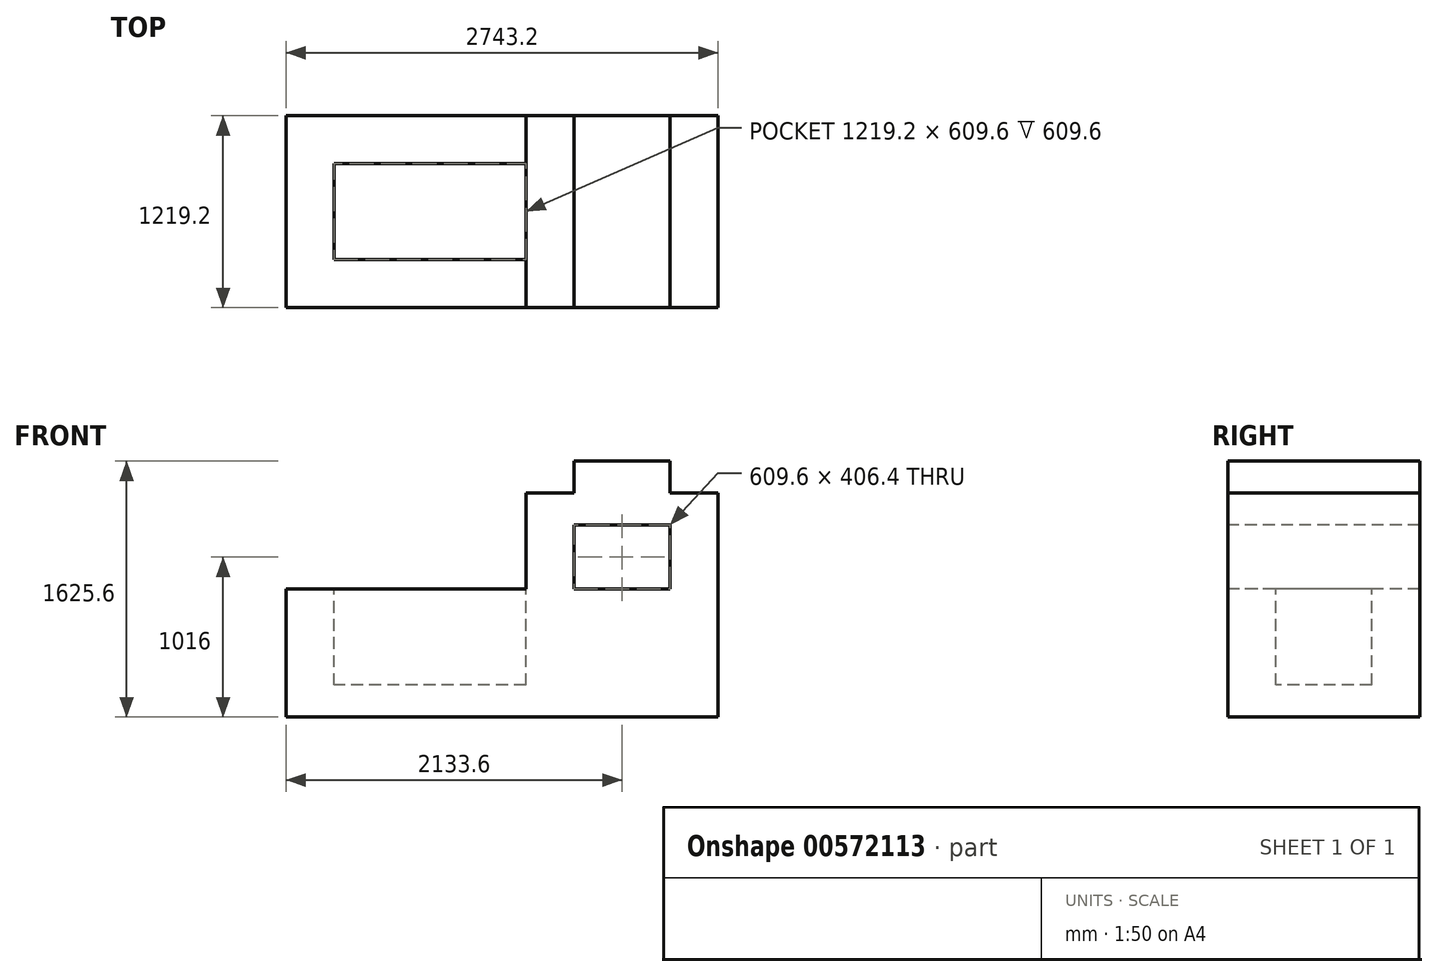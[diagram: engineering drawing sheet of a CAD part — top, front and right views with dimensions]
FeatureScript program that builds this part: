
annotation { "Feature Type Name" : "Feature", "Feature Type Description" : "" }
export const myFeature = defineFeature(function(context is Context, id is Id, definition is map)
    precondition{}
    {
        {
            var Q0;
            Q0=qCreatedBy(makeId("Front.planeOp"),FACE);
            var sketch = newSketch(context, id + "F0", { "sketchPlane" : qUnion([Q0])});
            skLineSegment(sketch, "E0.bottom", {"start": v(0, 0) * mm, "end": v(2743.2, 0) * mm});
            skLineSegment(sketch, "E0.top", {"start": v(0, 1625.6) * mm, "end": v(2743.2, 1625.6) * mm});
            skLineSegment(sketch, "E0.left", {"start": v(0, 0) * mm, "end": v(0, 1625.6) * mm});
            skLineSegment(sketch, "E0.right", {"start": v(2743.2, 0) * mm, "end": v(2743.2, 1625.6) * mm});
            skSolve(sketch);
        }
        {
            var Q0;
            Q0=makeQuery(id+"F0.imprint","IMPRINT",FACE,{"disambiguationData":[TD([[makeQuery(id+"F0.imprint","IMPRINT",EDGE,{"derivedFrom":sQuery(id+"F0.wireOp",EDGE,"E0.bottom")}),1.0]])]});
            extrude(context, id + "F1", {"entities" : qUnion([Q0]), "depth" : 1219.2 * mm, "offsetDistance" : 25.4 * mm});
        }
        {
            var Q0;
            Q0=makeQuery(id+"F1.opExtrude","CAP_FACE",FACE,{"disambiguationData":[OSD([sQuery(id+"F0.wireOp",EDGE,"E0.bottom"),sQuery(id+"F0.wireOp",EDGE,"E0.top"),sQuery(id+"F0.wireOp",EDGE,"E0.left"),sQuery(id+"F0.wireOp",EDGE,"E0.right")])],"isStart":false});
            var sketch = newSketch(context, id + "F2", { "sketchPlane" : qUnion([Q0])});
            skLineSegment(sketch, "E1", {"start": v(0, 812.8) * mm, "end": v(1524, 812.8) * mm});
            skLineSegment(sketch, "E2", {"start": v(1524, 812.8) * mm, "end": v(1524, 1625.6) * mm});
            skSolve(sketch);
        }
        {
            var Q0;
            {var subQ0=sQuery(id+"F2.wireOp",EDGE,"E1");Q0=makeQuery(id+"F2.imprint","IMPRINT",FACE,{"disambiguationData":[TD([[makeQuery(id+"F2.imprint","IMPRINT",EDGE,{"derivedFrom":subQ0}),1.0]])]});}
            extrude(context, id + "F3", {"entities" : qUnion([Q0]), "operationType" : NewBodyOperationType.REMOVE, "oppositeDirection" : true, "depth" : 1219.2 * mm, "offsetDistance" : 25.4 * mm});
        }
        {
            var Q0;
            Q0=makeQuery(id+"F1.opExtrude","CAP_FACE",FACE,{"disambiguationData":[OSD([sQuery(id+"F0.wireOp",EDGE,"E0.bottom"),sQuery(id+"F0.wireOp",EDGE,"E0.top"),sQuery(id+"F0.wireOp",EDGE,"E0.left"),sQuery(id+"F0.wireOp",EDGE,"E0.right")])],"isStart":false});
            var sketch = newSketch(context, id + "F4", { "sketchPlane" : qUnion([Q0])});
            skLineSegment(sketch, "E3", {"start": v(1524, 1422.4) * mm, "end": v(1828.8, 1422.4) * mm});
            skLineSegment(sketch, "E4", {"start": v(1828.8, 1422.4) * mm, "end": v(1828.8, 1625.6) * mm});
            skSolve(sketch);
        }
        {
            var Q0;
            {var subQ0=sQuery(id+"F4.wireOp",EDGE,"E3");Q0=makeQuery(id+"F4.imprint","IMPRINT",FACE,{"disambiguationData":[TD([[makeQuery(id+"F4.imprint","IMPRINT",EDGE,{"derivedFrom":subQ0}),1.0]])]});}
            extrude(context, id + "F5", {"entities" : qUnion([Q0]), "operationType" : NewBodyOperationType.REMOVE, "oppositeDirection" : true, "depth" : 1219.2 * mm, "offsetDistance" : 25.4 * mm});
        }
        {
            var Q0;
            Q0=makeQuery(id+"F1.opExtrude","CAP_FACE",FACE,{"disambiguationData":[OSD([sQuery(id+"F0.wireOp",EDGE,"E0.bottom"),sQuery(id+"F0.wireOp",EDGE,"E0.top"),sQuery(id+"F0.wireOp",EDGE,"E0.left"),sQuery(id+"F0.wireOp",EDGE,"E0.right")])],"isStart":false});
            var sketch = newSketch(context, id + "F6", { "sketchPlane" : qUnion([Q0])});
            skLineSegment(sketch, "E5", {"start": v(2743.2, 1422.4) * mm, "end": v(2438.4, 1422.4) * mm});
            skLineSegment(sketch, "E6", {"start": v(2438.4, 1422.4) * mm, "end": v(2438.4, 1625.6) * mm});
            skSolve(sketch);
        }
        {
            var Q0;
            {var subQ0=sQuery(id+"F6.wireOp",EDGE,"E5");Q0=makeQuery(id+"F6.imprint","IMPRINT",FACE,{"disambiguationData":[TD([[makeQuery(id+"F6.imprint","IMPRINT",EDGE,{"derivedFrom":subQ0}),-1.0]])]});}
            extrude(context, id + "F7", {"entities" : qUnion([Q0]), "operationType" : NewBodyOperationType.REMOVE, "oppositeDirection" : true, "depth" : 1219.2 * mm, "offsetDistance" : 25.4 * mm});
        }
        {
            var Q0;
            Q0=makeQuery(id+"F1.opExtrude","CAP_FACE",FACE,{"disambiguationData":[OSD([sQuery(id+"F0.wireOp",EDGE,"E0.bottom"),sQuery(id+"F0.wireOp",EDGE,"E0.top"),sQuery(id+"F0.wireOp",EDGE,"E0.left"),sQuery(id+"F0.wireOp",EDGE,"E0.right")])],"isStart":false});
            var sketch = newSketch(context, id + "F8", { "sketchPlane" : qUnion([Q0])});
            skLineSegment(sketch, "E7", {"start": v(2438.4, 1422.4) * mm, "end": v(2438.4, 1219.2) * mm});
            skLineSegment(sketch, "E8.bottom", {"start": v(2438.4, 1219.2) * mm, "end": v(1828.8, 1219.2) * mm});
            skLineSegment(sketch, "E8.top", {"start": v(2438.4, 812.8) * mm, "end": v(1828.8, 812.8) * mm});
            skLineSegment(sketch, "E8.left", {"start": v(2438.4, 1219.2) * mm, "end": v(2438.4, 812.8) * mm});
            skLineSegment(sketch, "E8.right", {"start": v(1828.8, 1219.2) * mm, "end": v(1828.8, 812.8) * mm});
            skSolve(sketch);
        }
        {
            var Q0;
            Q0=makeQuery(id+"F8.imprint","IMPRINT",FACE,{"disambiguationData":[TD([[makeQuery(id+"F8.imprint","IMPRINT",EDGE,{"derivedFrom":sQuery(id+"F8.wireOp",EDGE,"E8.bottom")}),1.0]])]});
            extrude(context, id + "F9", {"entities" : qUnion([Q0]), "operationType" : NewBodyOperationType.REMOVE, "oppositeDirection" : true, "depth" : 1219.2 * mm, "offsetDistance" : 25.4 * mm});
        }
        {
            var Q0;
            Q0=makeQuery(id+"F3.boolean.opBoolean","COPY",FACE,{"derivedFrom":makeQuery(id+"F3.opExtrude","SWEPT_FACE",FACE,{"disambiguationData":[OSD([sQuery(id+"F2.wireOp",EDGE,"E1")])]})});
            var sketch = newSketch(context, id + "F10", { "sketchPlane" : qUnion([Q0])});
            skLineSegment(sketch, "E9", {"start": v(1524, 0) * mm, "end": v(1524, -304.8) * mm});
            skLineSegment(sketch, "E10.bottom", {"start": v(1524, -304.8) * mm, "end": v(304.8, -304.8) * mm});
            skLineSegment(sketch, "E10.top", {"start": v(1524, -914.4) * mm, "end": v(304.8, -914.4) * mm});
            skLineSegment(sketch, "E10.left", {"start": v(1524, -304.8) * mm, "end": v(1524, -914.4) * mm});
            skLineSegment(sketch, "E10.right", {"start": v(304.8, -304.8) * mm, "end": v(304.8, -914.4) * mm});
            skSolve(sketch);
        }
        {
            var Q0;
            Q0=makeQuery(id+"F10.imprint","IMPRINT",FACE,{"disambiguationData":[TD([[makeQuery(id+"F10.imprint","IMPRINT",EDGE,{"derivedFrom":sQuery(id+"F10.wireOp",EDGE,"E10.bottom")}),1.0]])]});
            extrude(context, id + "F11", {"entities" : qUnion([Q0]), "operationType" : NewBodyOperationType.REMOVE, "oppositeDirection" : true, "depth" : 609.6 * mm, "offsetDistance" : 25.4 * mm});
        }
    });
